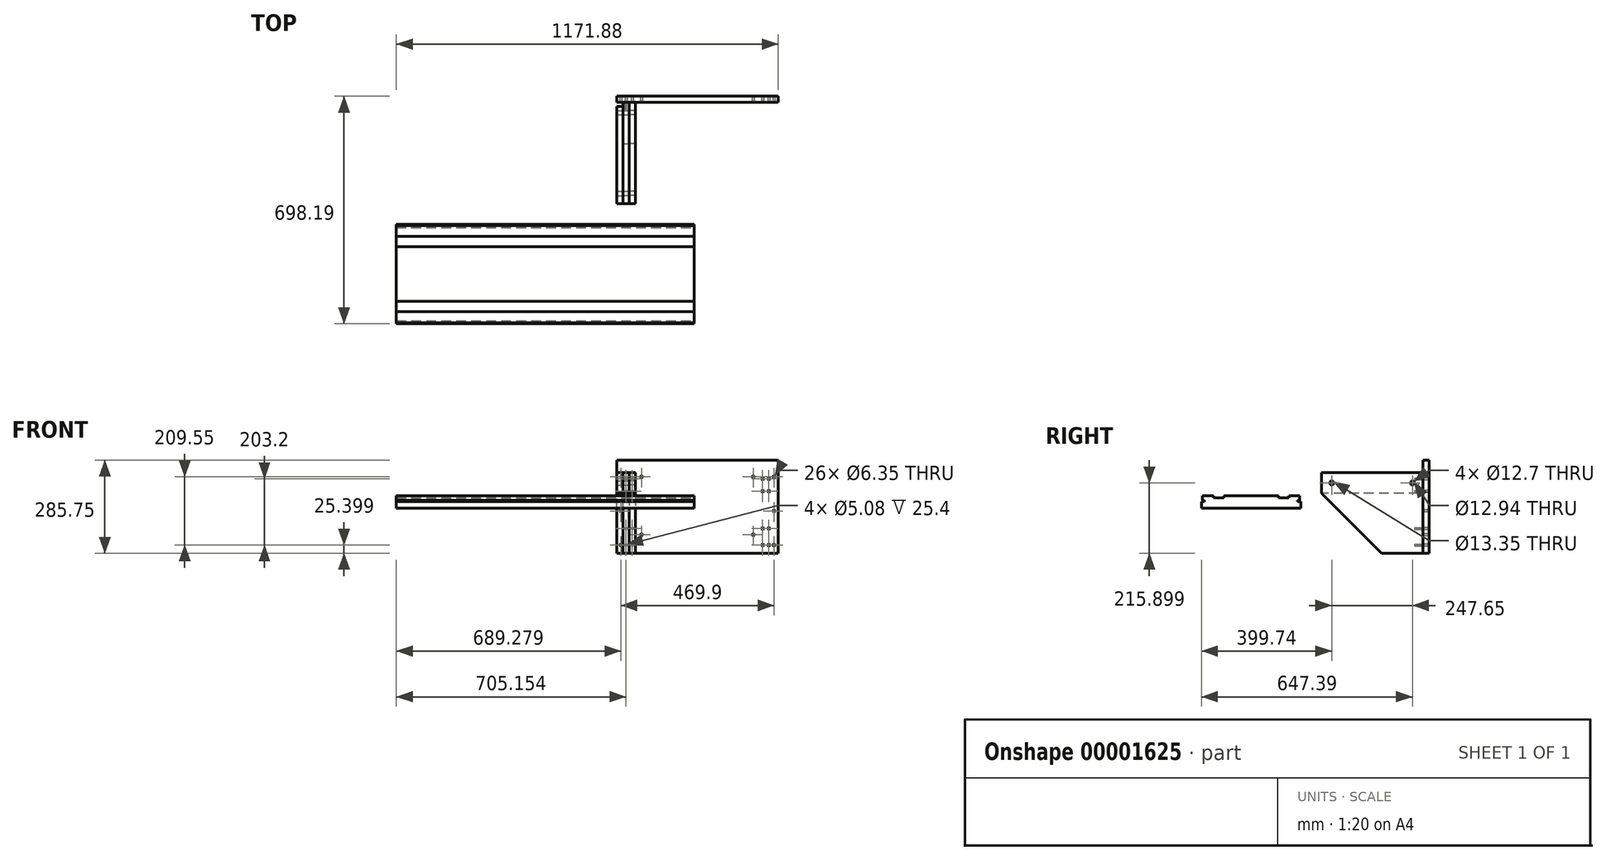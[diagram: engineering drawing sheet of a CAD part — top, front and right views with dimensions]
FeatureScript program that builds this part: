
annotation { "Feature Type Name" : "Feature", "Feature Type Description" : "" }
export const myFeature = defineFeature(function(context is Context, id is Id, definition is map)
    precondition{}
    {
        {
            var Q0;
            Q0=qCreatedBy(makeId("Front.planeOp"),FACE);
            var sketch = newSketch(context, id + "F0", { "sketchPlane" : qUnion([Q0])});
            skLineSegment(sketch, "E0.bottom", {"start": v(-237.82, -138.37) * mm, "end": v(257.48, -138.37) * mm});
            skLineSegment(sketch, "E0.top", {"start": v(-237.82, 147.38) * mm, "end": v(257.48, 147.38) * mm});
            skLineSegment(sketch, "E0.left", {"start": v(-237.82, -138.37) * mm, "end": v(-237.82, 147.38) * mm});
            skLineSegment(sketch, "E0.right", {"start": v(257.48, -138.37) * mm, "end": v(257.48, 147.38) * mm});
            skSolve(sketch);
        }
        {
            var Q0;
            Q0 = qSketchRegion(id + "F0", true);
            extrude(context, id + "F1", {"entities" : qUnion([Q0]), "depth" : 19.05 * mm});
        }
        {
            var Q0;
            Q0=makeQuery(id+"F1.opExtrude","CAP_FACE",FACE,{"disambiguationData":[OSD([sQuery(id+"F0.wireOp",EDGE,"E0.bottom"),sQuery(id+"F0.wireOp",EDGE,"E0.top"),sQuery(id+"F0.wireOp",EDGE,"E0.left"),sQuery(id+"F0.wireOp",EDGE,"E0.right")])],"isStart":false});
            var sketch = newSketch(context, id + "F2", { "sketchPlane" : qUnion([Q0])});
            skLineSegment(sketch, "E1", {"start": v(257.48, 96.58) * mm, "end": v(78.9, 96.58) * mm, "construction": true});
            skLineSegment(sketch, "E2", {"start": v(257.48, 90.23) * mm, "end": v(74.75, 90.23) * mm, "construction": true});
            skLineSegment(sketch, "E3", {"start": v(257.48, 52.13) * mm, "end": v(106.79, 52.13) * mm, "construction": true});
            skLineSegment(sketch, "E4", {"start": v(257.48, -8.2) * mm, "end": v(71, -8.2) * mm, "construction": true});
            skLineSegment(sketch, "E5", {"start": v(244.78, 142.99) * mm, "end": v(244.78, -128.7) * mm, "construction": true});
            skLineSegment(sketch, "E6", {"start": v(228.9, 135.56) * mm, "end": v(228.9, -112.87) * mm, "construction": true});
            skLineSegment(sketch, "E7", {"start": v(209.85, 129.62) * mm, "end": v(209.85, -115.34) * mm, "construction": true});
            skLineSegment(sketch, "E8", {"start": v(181.28, 126.16) * mm, "end": v(181.28, -118.8) * mm, "construction": true});
            skLineSegment(sketch, "E9", {"start": v(257.48, -112.97) * mm, "end": v(104.03, -112.97) * mm, "construction": true});
            skLineSegment(sketch, "E10", {"start": v(257.48, -81.22) * mm, "end": v(72.36, -81.22) * mm, "construction": true});
            skLineSegment(sketch, "E11", {"start": v(257.48, -62.17) * mm, "end": v(127.78, -62.17) * mm, "construction": true});
            skCircle(sketch, "E12", {"center": v(244.78, -112.97) * mm, "radius": 3.18 * mm});
            skCircle(sketch, "E13", {"center": v(228.9, -112.87) * mm, "radius": 3.18 * mm});
            skCircle(sketch, "E14", {"center": v(209.85, -112.97) * mm, "radius": 3.18 * mm});
            skCircle(sketch, "E15", {"center": v(181.28, -81.22) * mm, "radius": 3.18 * mm});
            skCircle(sketch, "E16", {"center": v(209.85, -62.17) * mm, "radius": 3.18 * mm});
            skCircle(sketch, "E17", {"center": v(228.9, -62.17) * mm, "radius": 3.18 * mm});
            skCircle(sketch, "E18", {"center": v(244.78, -8.2) * mm, "radius": 3.18 * mm});
            skCircle(sketch, "E19", {"center": v(228.9, 52.13) * mm, "radius": 3.18 * mm});
            skCircle(sketch, "E20", {"center": v(228.9, 90.23) * mm, "radius": 3.18 * mm});
            skCircle(sketch, "E21", {"center": v(209.85, 52.13) * mm, "radius": 3.18 * mm});
            skCircle(sketch, "E22", {"center": v(244.78, 96.58) * mm, "radius": 3.18 * mm});
            skCircle(sketch, "E23", {"center": v(181.28, 96.58) * mm, "radius": 3.18 * mm});
            skLineSegment(sketch, "E24", {"start": v(9.83, -138.37) * mm, "end": v(9.83, 147.38) * mm, "construction": true});
            skCircle(sketch, "E25.0.MirrorC", {"center": v(-225.12, -112.97) * mm, "radius": 3.18 * mm});
            skCircle(sketch, "E25.1.MirrorC", {"center": v(-190.2, -62.17) * mm, "radius": 3.18 * mm});
            skCircle(sketch, "E25.3.MirrorC", {"center": v(-209.25, 90.23) * mm, "radius": 3.18 * mm});
            skCircle(sketch, "E25.4.MirrorC", {"center": v(-190.2, -112.97) * mm, "radius": 3.18 * mm});
            skCircle(sketch, "E25.5.MirrorC", {"center": v(-161.62, -81.22) * mm, "radius": 3.18 * mm});
            skCircle(sketch, "E25.7.MirrorC", {"center": v(-209.25, -62.17) * mm, "radius": 3.18 * mm});
            skCircle(sketch, "E25.9.MirrorC", {"center": v(-161.62, 96.58) * mm, "radius": 3.18 * mm});
            skCircle(sketch, "E25.11.MirrorC", {"center": v(-225.12, 96.58) * mm, "radius": 3.18 * mm});
            skCircle(sketch, "E25.12.MirrorC", {"center": v(-209.25, 52.13) * mm, "radius": 3.18 * mm});
            skCircle(sketch, "E25.13.MirrorC", {"center": v(-209.25, -112.87) * mm, "radius": 3.18 * mm});
            skCircle(sketch, "E25.14.MirrorC", {"center": v(-190.2, 52.13) * mm, "radius": 3.18 * mm});
            skCircle(sketch, "E25.15.MirrorC", {"center": v(-225.12, -8.2) * mm, "radius": 3.18 * mm});
            skCircle(sketch, "E26", {"center": v(209.85, 90.23) * mm, "radius": 3.18 * mm});
            skCircle(sketch, "E27.0.MirrorC", {"center": v(-190.2, 90.23) * mm, "radius": 3.18 * mm});
            skSolve(sketch);
        }
        {
            var Q0;
            Q0 = qSketchRegion(id + "F2", true);
            extrude(context, id + "F3", {"entities" : qUnion([Q0]), "operationType" : NewBodyOperationType.REMOVE, "endBound" : BoundingType.UP_TO_NEXT, "oppositeDirection" : true, "depth" : 25.4 * mm});
        }
        {
            var Q0;
            Q0=makeQuery(id+"F1.opExtrude","CAP_FACE",FACE,{"disambiguationData":[OSD([sQuery(id+"F0.wireOp",EDGE,"E0.bottom"),sQuery(id+"F0.wireOp",EDGE,"E0.top"),sQuery(id+"F0.wireOp",EDGE,"E0.left"),sQuery(id+"F0.wireOp",EDGE,"E0.right")])],"isStart":false});
            var sketch = newSketch(context, id + "F4", { "sketchPlane" : qUnion([Q0])});
            skLineSegment(sketch, "E28.bottom", {"start": v(-218.77, -138.37) * mm, "end": v(-199.72, -138.37) * mm});
            skLineSegment(sketch, "E28.top", {"start": v(-218.77, 109.28) * mm, "end": v(-199.72, 109.28) * mm});
            skLineSegment(sketch, "E28.left", {"start": v(-218.77, -138.37) * mm, "end": v(-218.77, 109.28) * mm});
            skLineSegment(sketch, "E28.right", {"start": v(-199.72, -138.37) * mm, "end": v(-199.72, 109.28) * mm});
            skSolve(sketch);
        }
        {
            var Q0;
            Q0 = qSketchRegion(id + "F4", true);
            extrude(context, id + "F5", {"entities" : qUnion([Q0]), "depth" : 311.15 * mm});
        }
        {
            var Q0;
            Q0=makeQuery(id+"F5.opExtrude","SWEPT_FACE",FACE,{"disambiguationData":[OSD([sQuery(id+"F4.wireOp",EDGE,"E28.right")])]});
            var sketch = newSketch(context, id + "F6", { "sketchPlane" : qUnion([Q0])});
            skLineSegment(sketch, "E29", {"start": v(-330.2, 45.78) * mm, "end": v(-146.05, -138.37) * mm});
            skLineSegment(sketch, "E30", {"start": v(-146.05, -138.37) * mm, "end": v(-330.2, -138.37) * mm});
            skLineSegment(sketch, "E31", {"start": v(-330.2, -138.37) * mm, "end": v(-330.2, 45.78) * mm});
            skCircle(sketch, "E32", {"center": v(-298.45, 77.53) * mm, "radius": 6.35 * mm});
            skCircle(sketch, "E33", {"center": v(-50.8, 77.53) * mm, "radius": 6.35 * mm});
            skSolve(sketch);
        }
        {
            var Q0;
            Q0=makeQuery(id+"F6.imprint","IMPRINT",FACE,{"disambiguationData":[TD([[makeQuery(id+"F6.imprint","IMPRINT",EDGE,{"derivedFrom":sQuery(id+"F6.wireOp",EDGE,"E29")}),-1.0]])]});
            var Q1;
            Q1=makeQuery(id+"F6.imprint","IMPRINT",FACE,{"disambiguationData":[TD([[makeQuery(id+"F6.imprint","IMPRINT",EDGE,{"derivedFrom":sQuery(id+"F6.wireOp",EDGE,"E32")}),1.0]])]});
            var Q2;
            Q2=makeQuery(id+"F6.imprint","IMPRINT",FACE,{"disambiguationData":[TD([[makeQuery(id+"F6.imprint","IMPRINT",EDGE,{"derivedFrom":sQuery(id+"F6.wireOp",EDGE,"E33")}),1.0]])]});
            extrude(context, id + "F7", {"entities" : qUnion([Q0, Q1, Q2]), "operationType" : NewBodyOperationType.REMOVE, "endBound" : BoundingType.THROUGH_ALL, "oppositeDirection" : true, "depth" : 25.4 * mm});
        }
        {
            var Q0;
            Q0=makeQuery(id+"F5.opExtrude","SWEPT_FACE",FACE,{"disambiguationData":[OSD([sQuery(id+"F4.wireOp",EDGE,"E28.right")])]});
            extrude(context, id + "F8", {"entities" : qUnion([Q0]), "depth" : 19.05 * mm});
        }
        {
            var Q0;
            Q0=makeQuery(id+"F5.opExtrude","CAP_FACE",FACE,{"disambiguationData":[OSD([sQuery(id+"F4.wireOp",EDGE,"E28.bottom"),sQuery(id+"F4.wireOp",EDGE,"E28.top"),sQuery(id+"F4.wireOp",EDGE,"E28.left"),sQuery(id+"F4.wireOp",EDGE,"E28.right")])],"isStart":true});
            var sketch = newSketch(context, id + "F9", { "sketchPlane" : qUnion([Q0])});
            skLineSegment(sketch, "E34", {"start": v(209.25, 109.28) * mm, "end": v(209.25, -138.37) * mm, "construction": true});
            skCircle(sketch, "E35", {"center": v(209.25, 52.13) * mm, "radius": 2.54 * mm});
            skCircle(sketch, "E36", {"center": v(209.25, 90.23) * mm, "radius": 2.54 * mm});
            skCircle(sketch, "E37", {"center": v(209.25, -112.97) * mm, "radius": 2.54 * mm});
            skCircle(sketch, "E38", {"center": v(209.25, -62.17) * mm, "radius": 2.54 * mm});
            skSolve(sketch);
        }
        {
            var Q0;
            Q0 = qSketchRegion(id + "F9", true);
            extrude(context, id + "F10", {"entities" : qUnion([Q0]), "operationType" : NewBodyOperationType.REMOVE, "oppositeDirection" : true, "depth" : 25.4 * mm});
        }
        {
            var Q0;
            Q0=makeQuery(id+"F5.opExtrude","CAP_FACE",FACE,{"disambiguationData":[OSD([sQuery(id+"F4.wireOp",EDGE,"E28.bottom"),sQuery(id+"F4.wireOp",EDGE,"E28.top"),sQuery(id+"F4.wireOp",EDGE,"E28.left"),sQuery(id+"F4.wireOp",EDGE,"E28.right")])],"isStart":false});
            var sketch = newSketch(context, id + "F11", { "sketchPlane" : qUnion([Q0])});
            skLineSegment(sketch, "E39.bottom", {"start": v(-218.77, 109.28) * mm, "end": v(-237.82, 109.28) * mm});
            skLineSegment(sketch, "E39.top", {"start": v(-218.77, 45.78) * mm, "end": v(-237.82, 45.78) * mm});
            skLineSegment(sketch, "E39.left", {"start": v(-218.77, 109.28) * mm, "end": v(-218.77, 45.78) * mm});
            skLineSegment(sketch, "E39.right", {"start": v(-237.82, 109.28) * mm, "end": v(-237.82, 45.78) * mm});
            skSolve(sketch);
        }
        {
            var Q0;
            Q0=makeQuery(id+"F11.imprint","IMPRINT",FACE,{"disambiguationData":[TD([[makeQuery(id+"F11.imprint","IMPRINT",EDGE,{"derivedFrom":sQuery(id+"F11.wireOp",EDGE,"E39.bottom")}),1.0]])]});
            extrude(context, id + "F12", {"entities" : qUnion([Q0]), "oppositeDirection" : true, "depth" : 298.45 * mm});
        }
        {
            var Q0;
            Q0=makeQuery(id+"F5.opExtrude","SWEPT_FACE",FACE,{"disambiguationData":[OSD([sQuery(id+"F4.wireOp",EDGE,"E28.left")])]});
            var sketch = newSketch(context, id + "F13", { "sketchPlane" : qUnion([Q0])});
            skCircle(sketch, "E40", {"center": v(50.8, 77.53) * mm, "radius": 6.47 * mm});
            skCircle(sketch, "E41", {"center": v(298.45, 77.53) * mm, "radius": 6.67 * mm});
            skSolve(sketch);
        }
        {
            var Q0;
            Q0 = qSketchRegion(id + "F13", true);
            extrude(context, id + "F14", {"entities" : qUnion([Q0]), "operationType" : NewBodyOperationType.REMOVE, "depth" : 19.05 * mm});
        }
        {
            var Q0;
            Q0=qCreatedBy(makeId("Right.planeOp"),FACE);
            var sketch = newSketch(context, id + "F15", { "sketchPlane" : qUnion([Q0])});
            skLineSegment(sketch, "E42", {"start": v(-698.19, 0) * mm, "end": v(-393.39, 0) * mm});
            skLineSegment(sketch, "E43", {"start": v(-393.39, 0) * mm, "end": v(-393.39, 20.64) * mm});
            skLineSegment(sketch, "E44", {"start": v(-393.39, 20.64) * mm, "end": v(-402.91, 20.64) * mm});
            skLineSegment(sketch, "E45", {"start": v(-402.91, 20.64) * mm, "end": v(-402.91, 24.6) * mm});
            skLineSegment(sketch, "E46", {"start": v(-402.91, 24.6) * mm, "end": v(-396.56, 24.6) * mm});
            skLineSegment(sketch, "E47", {"start": v(-396.56, 24.6) * mm, "end": v(-396.56, 38.1) * mm});
            skLineSegment(sketch, "E48", {"start": v(-396.56, 38.1) * mm, "end": v(-429.9, 38.1) * mm});
            skLineSegment(sketch, "E49", {"start": v(-429.9, 38.1) * mm, "end": v(-429.9, 31.88) * mm});
            skLineSegment(sketch, "E50", {"start": v(-429.9, 31.88) * mm, "end": v(-461.65, 31.88) * mm});
            skLineSegment(sketch, "E51", {"start": v(-461.65, 31.88) * mm, "end": v(-461.65, 38.1) * mm});
            skLineSegment(sketch, "E52", {"start": v(-461.65, 38.1) * mm, "end": v(-629.92, 38.1) * mm});
            skLineSegment(sketch, "E53", {"start": v(-698.19, 20.64) * mm, "end": v(-698.19, 0) * mm});
            skLineSegment(sketch, "E54", {"start": v(-545.79, 0) * mm, "end": v(-545.79, 38.1) * mm, "construction": true});
            skLineSegment(sketch, "E55.0.MirrorCS", {"start": v(-661.67, 38.1) * mm, "end": v(-661.67, 31.88) * mm});
            skLineSegment(sketch, "E55.1.MirrorCS", {"start": v(-688.66, 20.64) * mm, "end": v(-688.66, 24.6) * mm});
            skLineSegment(sketch, "E55.2.MirrorCS", {"start": v(-698.19, 20.64) * mm, "end": v(-688.66, 20.64) * mm});
            skLineSegment(sketch, "E55.3.MirrorCS", {"start": v(-698.19, 0) * mm, "end": v(-698.19, 20.64) * mm});
            skLineSegment(sketch, "E55.4.MirrorCS", {"start": v(-688.66, 24.6) * mm, "end": v(-695.01, 24.6) * mm});
            skLineSegment(sketch, "E55.5.MirrorCS", {"start": v(-695.01, 38.1) * mm, "end": v(-661.67, 38.1) * mm});
            skLineSegment(sketch, "E55.6.MirrorCS", {"start": v(-695.01, 24.6) * mm, "end": v(-695.01, 38.1) * mm});
            skLineSegment(sketch, "E55.7.MirrorCS", {"start": v(-629.92, 31.88) * mm, "end": v(-629.92, 38.1) * mm});
            skLineSegment(sketch, "E55.8.MirrorCS", {"start": v(-661.67, 31.88) * mm, "end": v(-629.92, 31.88) * mm});
            skLineSegment(sketch, "E56.trimOffspring", {"start": v(-661.67, 38.1) * mm, "end": v(-695.01, 38.1) * mm});
            skPoint(sketch, "E57.orphan", {"position": v(-698.19, 38.1) * mm});
            skSolve(sketch);
        }
        {
            var Q0;
            Q0=makeQuery(id+"F15.imprint","IMPRINT",FACE,{"disambiguationData":[TD([[makeQuery(id+"F15.imprint","IMPRINT",EDGE,{"derivedFrom":sQuery(id+"F15.wireOp",EDGE,"E42")}),1.0]])]});
            extrude(context, id + "F16", {"entities" : qUnion([Q0]), "oppositeDirection" : true, "depth" : 914.4 * mm});
        }
    });
